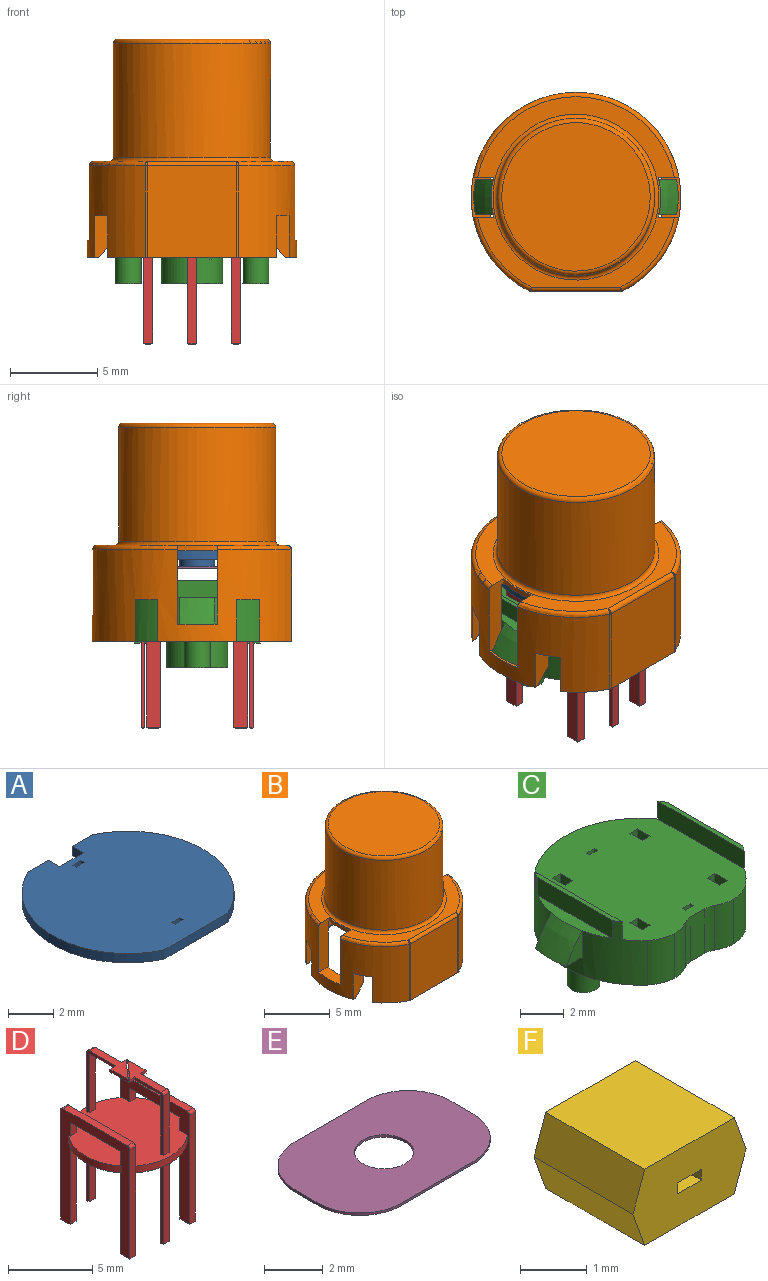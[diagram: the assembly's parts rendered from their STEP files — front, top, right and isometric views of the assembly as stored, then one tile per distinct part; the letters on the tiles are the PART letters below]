
ASSEMBLY  parts=6 mates=10
PART A: 20 faces, bbox 9.4x8.5x1 mm
  f0: plane 0.5x0.5mm, normal (0,1,0), area 0.3mm2, adj f1,f15,f16,f17
  f1: plane 0.5x0.2mm, normal (1,0,0), area 0.1mm2, adj f0,f2,f16,f17
  f2: plane 0.5x0.5mm, normal (0,-1,0), area 0.3mm2, adj f1,f15,f16,f17
  f3: plane 0.5x0.2mm, normal (1,0,0), area 0.1mm2, adj f4,f13,f16,f17
  f4: plane 0.5x0.5mm, normal (0,-1,0), area 0.3mm2, adj f3,f5,f16,f17
  f5: plane 0.5x0.2mm, normal (-1,0,0), area 0.1mm2, adj f4,f13,f16,f17
  f6: plane 1.26x0.5mm, normal (0,1,0), area 0.6mm2, adj f7,f14,f16,f17
  f7: plane 0.7x0.5mm, normal (-1,0,0), area 0.4mm2, adj f6,f8,f16,f17
  f8: plane 1.5x0.5mm, normal (0,1,0), area 0.8mm2, adj f7,f9,f16,f17
  f9: plane 0.7x0.5mm, normal (1,0,0), area 0.4mm2, adj f8,f10,f16,f17
  f10: plane 1.26x0.5mm, normal (0,1,0), area 0.6mm2, adj f9,f11,f16,f17
  f11: cylinder r=4.7mm len=8.5mm, axis (0,0,-1), area 5.3mm2, adj f10,f12,f16,f17
  f12: plane 4x0.5mm, normal (0,-1,0), area 2mm2, adj f11,f14,f16,f17
  f13: plane 0.5x0.5mm, normal (0,1,0), area 0.3mm2, adj f3,f5,f16,f17
  f14: cylinder r=4.7mm len=8.5mm, axis (0,0,-1), area 5.3mm2, adj f6,f12,f16,f17
  f15: plane 0.5x0.2mm, normal (-1,0,0), area 0.1mm2, adj f0,f2,f16,f17
  f16: plane 9.4x8.5mm, normal (0,0,1), area 65.7mm2, adj f0,f1,f2,f3,f4,f5,f6,f7
  f17: plane 9.4x8.5mm, normal (0,0,-1), area 62.6mm2, adj f0,f1,f2,f3,f4,f5,f6,f7
  f18: cylinder r=1mm len=2mm, axis (0,0,1), area 3.1mm2, adj f17,f19
  f19: plane 2x2mm, normal (0,0,-1), area 3.1mm2, adj f18
PART B: 55 faces, bbox 12.8x12.4x12.6 mm
  f0: cylinder r=5mm len=4.2mm, axis (0,0,1), area 15.5mm2, adj f8,f10,f18,f22,f30,f34,f35,f36
  f1: cylinder r=5mm len=4.2mm, axis (0,0,1), area 15.5mm2, adj f6,f10,f13,f18,f29,f40,f41,f42
  f2: cylinder r=6mm len=12mm, axis (0,0,1), area 134.9mm2, adj f3,f4,f5,f12,f13,f16,f22,f23
  f3: plane 4.57x0.7mm, normal (0,0,-1), area 0.9mm2, adj f2,f8,f31,f35
  f4: plane 4.57x0.7mm, normal (0,0,-1), area 0.9mm2, adj f2,f6,f38,f41
  f5: plane 9.69x2.49mm, normal (0,0,-1), area 2.2mm2, adj f2,f7,f9,f32,f39
  f6: bspline ~5.22x1.33mm, area 6mm2, adj f1,f4,f11,f25,f38,f41
  f7: bspline ~4.58x2.74mm, area 5.9mm2, adj f5,f9,f11,f39
  f8: bspline ~5.22x1.33mm, area 6mm2, adj f0,f3,f11,f24,f31,f35
  f9: bspline ~4.58x2.74mm, area 5.9mm2, adj f5,f7,f11,f32
  f10: plane 4.75x4.2mm, normal (0,1,0), area 19.9mm2, adj f0,f1,f18,f28
  f11: cylinder r=5mm len=9.73mm, axis (0,0,1), area 44.7mm2, adj f6,f7,f8,f9,f12,f18,f23,f31
  f12: plane 4.52x1.2mm, normal (0,-1,0), area 4.6mm2, adj f2,f11,f17,f18,f25,f27,f51
  f13: plane 4.52x1.2mm, normal (0,1,0), area 4.6mm2, adj f1,f2,f17,f18,f25,f27,f45
  f14: cylinder r=3.5mm len=7mm, axis (0,0,1), area 138.5mm2, adj f18,f21
  f15: plane 5.25x5.11mm, normal (0,-1,0), area 26.9mm2, adj f16,f44,f47,f48
  f16: plane 9.7x1.9mm, normal (0,0,-1), area 2.1mm2, adj f2,f15,f28,f29,f30,f34,f42,f44
  f17: plane 11.27x10.9mm, normal (0,0,1), area 26.7mm2, adj f12,f13,f22,f23,f26,f27,f45,f48
  f18: plane 9.73x8.87mm, normal (0,0,-1), area 35.8mm2, adj f0,f1,f10,f11,f12,f13,f14,f22
  f19: cylinder r=4.5mm len=9mm, axis (0,0,-1), area 183.8mm2, adj f43,f52
  f20: plane 8.5x8.5mm, normal (0,0,1), area 56.7mm2, adj f43
  f21: plane 7x7mm, normal (0,0,-1), area 38.5mm2, adj f14
  f22: plane 4.52x1.2mm, normal (0,1,0), area 4.6mm2, adj f0,f2,f17,f18,f24,f26,f50
  f23: plane 4.52x1.2mm, normal (0,-1,0), area 4.6mm2, adj f2,f11,f17,f18,f24,f26,f51
  f24: plane 2.3x1.14mm, normal (0,0,1), area 2.3mm2, adj f2,f8,f22,f23
  f25: plane 2.3x1.14mm, normal (0,0,1), area 2.3mm2, adj f2,f6,f12,f13
  f26: cylinder r=4.85mm len=2.3mm, axis (0,0,1), area 0.7mm2, adj f17,f18,f22,f23
  f27: cylinder r=4.85mm len=2.3mm, axis (0,0,1), area 0.7mm2, adj f12,f13,f17,f18
  f28: plane 5.16x1mm, normal (0,0.78,-0.62), area 6.3mm2, adj f10,f16,f29,f30
  f29: bspline ~2.39x2.14mm, area 2.6mm2, adj f1,f16,f28,f42
  f30: bspline ~2.39x2.14mm, area 2.6mm2, adj f0,f16,f28,f34
  f31: plane 2.43x1.13mm, normal (0,1,0), area 2.2mm2, adj f2,f3,f8,f11,f33
  f32: plane 2.46x1.38mm, normal (0,-1,0), area 2.6mm2, adj f2,f5,f9,f11,f33
  f33: plane 2.04x1.3mm, normal (0,0,-1), area 1.5mm2, adj f2,f11,f31,f32
  f34: plane 2.46x1.38mm, normal (0,1,0), area 2.6mm2, adj f0,f2,f16,f30,f36
  f35: plane 2.43x1.13mm, normal (0,-1,0), area 2.2mm2, adj f0,f2,f3,f8,f36
  f36: plane 2.04x1.3mm, normal (0,0,-1), area 1.5mm2, adj f0,f2,f34,f35
  f37: plane 2.04x1.3mm, normal (0,0,-1), area 1.5mm2, adj f2,f11,f38,f39
  f38: plane 2.43x1.13mm, normal (0,1,0), area 2.2mm2, adj f2,f4,f6,f11,f37
  f39: plane 2.46x1.38mm, normal (0,-1,0), area 2.6mm2, adj f2,f5,f7,f11,f37
  f40: plane 2.04x1.3mm, normal (0,0,-1), area 1.5mm2, adj f1,f2,f41,f42
  f41: plane 2.43x1.13mm, normal (0,-1,0), area 2.2mm2, adj f1,f2,f4,f6,f40
  f42: plane 2.46x1.38mm, normal (0,1,0), area 2.6mm2, adj f1,f2,f16,f29,f40
  f43: torus R=4.25mm, axis (0,0,1), area 10.9mm2, adj f19,f20
  f44: cylinder r=0.25mm len=5.25mm, axis (0,0,1), area 0.6mm2, adj f2,f15,f16,f46
  f45: torus R=5.75mm, axis (0,0,-1), area 2.1mm2, adj f2,f13,f17,f46
  f46: sphere r=0.25mm, area 0mm2, adj f44,f45,f48
  f47: cylinder r=0.25mm len=5.25mm, axis (0,0,1), area 0.6mm2, adj f2,f15,f16,f49
  f48: cylinder r=0.25mm len=5.11mm, axis (-1,0,0), area 2mm2, adj f15,f17,f46,f49
  f49: sphere r=0.25mm, area 0mm2, adj f47,f48,f50
  f50: torus R=5.75mm, axis (0,0,-1), area 2.1mm2, adj f2,f17,f22,f49
  f51: torus R=5.75mm, axis (0,0,-1), area 6.4mm2, adj f2,f12,f17,f23
  f52: torus R=4.75mm, axis (0,0,-1), area 11.3mm2, adj f17,f19
  f53: plane 4.5x1.5mm, normal (0,-1,0), area 6.8mm2, adj f11,f18,f54
  f54: plane 4.5x0.54mm, normal (0,0,-1), area 1.6mm2, adj f11,f53
PART C: 92 faces, bbox 11.7x9x5 mm
  f0: plane 9x7.92mm, normal (0,0,1), area 62mm2, adj f2,f3,f4,f5,f6,f7,f8,f9
  f1: plane 4.85x0.65mm, normal (0,0,1), area 2.1mm2, adj f17,f18,f87
  f2: plane 1x0.5mm, normal (0,-1,0), area 0.5mm2, adj f0,f34,f36,f67
  f3: plane 1x0.5mm, normal (0,1,0), area 0.5mm2, adj f0,f38,f40,f67
  f4: plane 1x0.5mm, normal (0,1,0), area 0.5mm2, adj f0,f42,f44,f67
  f5: plane 1x0.5mm, normal (0,-1,0), area 0.5mm2, adj f0,f46,f48,f67
  f6: plane 1x0.5mm, normal (0,-1,0), area 0.5mm2, adj f0,f7,f9,f67
  f7: plane 1x0.2mm, normal (1,0,0), area 0.2mm2, adj f0,f6,f8,f67
  f8: plane 1x0.5mm, normal (0,1,0), area 0.5mm2, adj f0,f7,f9,f67
  f9: plane 1x0.2mm, normal (-1,0,0), area 0.2mm2, adj f0,f6,f8,f67
  f10: plane 1x0.5mm, normal (0,-1,0), area 0.5mm2, adj f0,f11,f13,f67
  f11: plane 1x0.2mm, normal (1,0,0), area 0.2mm2, adj f0,f10,f12,f67
  f12: plane 1x0.5mm, normal (0,1,0), area 0.5mm2, adj f0,f11,f13,f67
  f13: plane 1x0.2mm, normal (-1,0,0), area 0.2mm2, adj f0,f10,f12,f67
  f14: plane 2x1.1mm, normal (0,0,-1), area 2mm2, adj f15,f18,f60,f61
  f15: revolved ~2.41x1.5mm, area 3.7mm2, adj f14,f19,f60,f61
  f16: plane 2x1.1mm, normal (0,0,-1), area 2mm2, adj f17,f18,f58,f59
  f17: revolved ~2.41x1.5mm, area 3.7mm2, adj f1,f16,f58,f59
  f18: cylinder r=4.85mm len=9.7mm, axis (0,0,-1), area 54.6mm2, adj f0,f1,f14,f16,f19,f20,f28,f30
  f19: plane 4.85x0.65mm, normal (0,0,1), area 2.1mm2, adj f15,f18,f90
  f20: plane 9.7x9mm, normal (0,0,-1), area 55.3mm2, adj f18,f21,f23,f25,f27,f28,f29,f30
  f21: cylinder r=1.75mm len=3.5mm, axis (0,0,-1), area 16.5mm2, adj f20,f22
  f22: plane 3.5x3.5mm, normal (0,0,-1), area 9.6mm2, adj f21
  f23: cylinder r=0.75mm len=1.5mm, axis (0,0,-1), area 7.1mm2, adj f20,f24
  f24: plane 1.5x1.5mm, normal (0,0,-1), area 1.8mm2, adj f23
  f25: cylinder r=0.75mm len=1.5mm, axis (0,0,-1), area 7.1mm2, adj f20,f26
  f26: plane 1.5x1.5mm, normal (0,0,-1), area 1.8mm2, adj f25
  f27: plane 2.5x0.91mm, normal (0,-1,0), area 2.3mm2, adj f0,f20,f32,f33
  f28: cylinder r=2mm len=2.5mm, axis (0,0,-1), area 3.5mm2, adj f0,f18,f20,f29
  f29: cylinder r=2mm len=2.5mm, axis (0,0,1), area 2.5mm2, adj f0,f20,f28,f33
  f30: cylinder r=2mm len=2.5mm, axis (0,0,-1), area 3.5mm2, adj f0,f18,f20,f31
  f31: cylinder r=2mm len=2.5mm, axis (0,0,1), area 2.5mm2, adj f0,f20,f30,f32
  f32: cylinder r=1mm len=2.5mm, axis (0,0,1), area 1.3mm2, adj f0,f20,f27,f31
  f33: cylinder r=1mm len=2.5mm, axis (0,0,1), area 1.3mm2, adj f0,f20,f27,f29
  f34: plane 2.5x0.8mm, normal (1,0,0), area 1.7mm2, adj f0,f2,f20,f35,f37,f63,f66,f67
  f35: plane 2.5x0.5mm, normal (0,1,0), area 1.3mm2, adj f0,f20,f34,f36
  f36: plane 2.5x0.8mm, normal (-1,0,0), area 1.9mm2, adj f0,f2,f20,f35,f37,f62,f66,f67
  f37: plane 1x0.5mm, normal (0,-1,0), area 0.5mm2, adj f20,f34,f36,f66
  f38: plane 2.5x0.8mm, normal (1,0,0), area 1.7mm2, adj f0,f3,f20,f39,f41,f64,f66,f67
  f39: plane 1x0.5mm, normal (0,1,0), area 0.5mm2, adj f20,f38,f40,f66
  f40: plane 2.5x0.8mm, normal (-1,0,0), area 1.9mm2, adj f0,f3,f20,f39,f41,f62,f66,f67
  f41: plane 2.5x0.5mm, normal (0,-1,0), area 1.3mm2, adj f0,f20,f38,f40
  f42: plane 2.5x0.8mm, normal (1,0,0), area 1.9mm2, adj f0,f4,f20,f43,f45,f65,f66,f67
  f43: plane 1x0.5mm, normal (0,1,0), area 0.5mm2, adj f20,f42,f44,f66
  f44: plane 2.5x0.8mm, normal (-1,0,0), area 1.7mm2, adj f0,f4,f20,f43,f45,f64,f66,f67
  f45: plane 2.5x0.5mm, normal (0,-1,0), area 1.2mm2, adj f0,f20,f42,f44
  f46: plane 2.5x0.8mm, normal (1,0,0), area 1.9mm2, adj f0,f5,f20,f47,f49,f65,f66,f67
  f47: plane 2.5x0.5mm, normal (0,1,0), area 1.2mm2, adj f0,f20,f46,f48
  f48: plane 2.5x0.8mm, normal (-1,0,0), area 1.7mm2, adj f0,f5,f20,f47,f49,f63,f66,f67
  f49: plane 1x0.5mm, normal (0,-1,0), area 0.5mm2, adj f20,f46,f48,f66
  f50: plane 1x0.5mm, normal (0,-1,0), area 0.5mm2, adj f20,f51,f53,f66
  f51: plane 1x0.2mm, normal (1,0,0), area 0.2mm2, adj f20,f50,f52,f66
  f52: plane 1x0.5mm, normal (0,1,0), area 0.5mm2, adj f20,f51,f53,f66
  f53: plane 1x0.2mm, normal (-1,0,0), area 0.2mm2, adj f20,f50,f52,f66
  f54: plane 1x0.5mm, normal (0,-1,0), area 0.5mm2, adj f20,f55,f57,f66
  f55: plane 1x0.2mm, normal (1,0,0), area 0.2mm2, adj f20,f54,f56,f66
  f56: plane 1x0.5mm, normal (0,1,0), area 0.5mm2, adj f20,f55,f57,f66
  f57: plane 1x0.2mm, normal (-1,0,0), area 0.2mm2, adj f20,f54,f56,f66
  f58: plane 1.54x1.06mm, normal (0,-1,0), area 0.8mm2, adj f16,f17,f18
  f59: plane 1.54x1.06mm, normal (0,1,0), area 0.8mm2, adj f16,f17,f18
  f60: plane 1.54x1.06mm, normal (0,1,0), area 0.8mm2, adj f14,f15,f18
  f61: plane 1.54x1.06mm, normal (0,-1,0), area 0.8mm2, adj f14,f15,f18
  f62: cylinder r=3.54mm len=4.44mm, axis (0,0,1), area 2.4mm2, adj f36,f40,f66,f67
  f63: cylinder r=3.54mm len=4.5mm, axis (0,0,1), area 2.4mm2, adj f34,f48,f66,f67
  f64: cylinder r=3.54mm len=4.5mm, axis (0,0,1), area 2.4mm2, adj f38,f44,f66,f67
  f65: cylinder r=3.54mm len=4.44mm, axis (0,0,1), area 2.4mm2, adj f42,f46,f66,f67
  f66: plane 7.07x7.07mm, normal (0,0,1), area 38.3mm2, adj f34,f36,f37,f38,f39,f40,f42,f43
  f67: plane 7.07x7.07mm, normal (0,0,-1), area 38.3mm2, adj f2,f3,f4,f5,f6,f7,f8,f9
  f68: plane 0.1x0.1mm, normal (0,1,0), area 0mm2, adj f20,f69,f79,f80
  f69: plane 0.45x0.1mm, normal (1,0,0), area 0mm2, adj f20,f68,f70,f80
  f70: plane 0.45x0.1mm, normal (0,1,0), area 0mm2, adj f20,f69,f71,f80
  f71: plane 0.1x0.1mm, normal (1,0,0), area 0mm2, adj f20,f70,f72,f80
  f72: plane 0.45x0.1mm, normal (0,-1,0), area 0mm2, adj f20,f71,f73,f80
  f73: plane 0.45x0.1mm, normal (1,0,0), area 0mm2, adj f20,f72,f74,f80
  f74: plane 0.1x0.1mm, normal (0,-1,0), area 0mm2, adj f20,f73,f75,f80
  f75: plane 0.45x0.1mm, normal (-1,0,0), area 0mm2, adj f20,f74,f76,f80
  f76: plane 0.45x0.1mm, normal (0,-1,0), area 0mm2, adj f20,f75,f77,f80
  f77: plane 0.1x0.1mm, normal (-1,0,0), area 0mm2, adj f20,f76,f78,f80
  f78: plane 0.45x0.1mm, normal (0,1,0), area 0mm2, adj f20,f77,f79,f80
  f79: plane 0.45x0.1mm, normal (-1,0,0), area 0mm2, adj f20,f68,f78,f80
  f80: plane 1x1mm, normal (0,0,-1), area 0.2mm2, adj f68,f69,f70,f71,f72,f73,f74,f75
  f81: plane 0.1x0.1mm, normal (0,1,0), area 0mm2, adj f20,f82,f84,f85
  f82: plane 1x0.1mm, normal (1,0,0), area 0.1mm2, adj f20,f81,f83,f85
  f83: plane 0.1x0.1mm, normal (0,-1,0), area 0mm2, adj f20,f82,f84,f85
  f84: plane 1x0.1mm, normal (-1,0,0), area 0.1mm2, adj f20,f81,f83,f85
  f85: plane 1x0.1mm, normal (0,0,-1), area 0.1mm2, adj f81,f82,f83,f84
  f86: plane 5.6x1mm, normal (-1,0,0), area 5.6mm2, adj f0,f18,f88
  f87: plane 4.85x1mm, normal (1,0,0), area 4.9mm2, adj f1,f18,f88
  f88: plane 5.6x0.24mm, normal (0,0,1), area 1.3mm2, adj f18,f86,f87
  f89: plane 5.6x1mm, normal (1,0,0), area 5.6mm2, adj f0,f18,f91
  f90: plane 4.85x1mm, normal (-1,0,0), area 4.9mm2, adj f18,f19,f91
  f91: plane 5.6x0.24mm, normal (0,0,1), area 1.3mm2, adj f18,f89,f90
PART D: 92 faces, bbox 7.1x7.1x11 mm
  f0: plane 7.07x7.07mm, normal (0,0,-1), area 38.3mm2, adj f1,f2,f3,f4,f5,f7,f12,f14
  f1: cylinder r=3.54mm len=4.44mm, axis (0,0,1), area 2.4mm2, adj f0,f9,f12
  f2: cylinder r=3.54mm len=4.5mm, axis (0,0,1), area 2.4mm2, adj f0,f5,f9,f14
  f3: cylinder r=3.54mm len=4.5mm, axis (0,0,1), area 2.4mm2, adj f0,f5,f9,f14
  f4: cylinder r=3.54mm len=4.44mm, axis (0,0,1), area 2.4mm2, adj f0,f7,f9
  f5: plane 8.1x5.8mm, normal (-1,0,0), area 15.3mm2, adj f0,f2,f3,f6,f8,f9,f10,f11
  f6: plane 7.9x0.5mm, normal (0,-1,0), area 4mm2, adj f5,f7,f45,f86
  f7: plane 8.1x5.8mm, normal (1,0,0), area 15.8mm2, adj f0,f4,f6,f8,f9,f10,f11,f26
  f8: plane 1x0.5mm, normal (0,1,0), area 0.5mm2, adj f5,f7,f9,f71
  f9: plane 7.07x7.07mm, normal (0,0,1), area 38.3mm2, adj f1,f2,f3,f4,f5,f7,f8,f10
  f10: plane 1x0.5mm, normal (0,-1,0), area 0.5mm2, adj f5,f7,f9,f71
  f11: plane 7.9x0.5mm, normal (0,1,0), area 4mm2, adj f5,f7,f50,f87
  f12: plane 8.1x5.8mm, normal (-1,0,0), area 15.8mm2, adj f0,f1,f9,f13,f15,f16,f17,f30
  f13: plane 1x0.5mm, normal (0,-1,0), area 0.5mm2, adj f9,f12,f14,f70
  f14: plane 8.1x5.8mm, normal (1,0,0), area 15.3mm2, adj f0,f2,f3,f9,f13,f15,f16,f17
  f15: plane 7.9x0.5mm, normal (0,1,0), area 3.9mm2, adj f12,f14,f54,f89
  f16: plane 7.9x0.5mm, normal (0,-1,0), area 3.9mm2, adj f12,f14,f57,f88
  f17: plane 1x0.5mm, normal (0,1,0), area 0.5mm2, adj f9,f12,f14,f70
  f18: plane 4.25x0.5mm, normal (0,1,0), area 2.1mm2, adj f9,f19,f21,f91
  f19: plane 4.5x2.4mm, normal (-1,0,0), area 1.3mm2, adj f9,f18,f20,f72,f73,f74,f85,f91
  f20: plane 4.3x0.5mm, normal (0,-1,0), area 2.1mm2, adj f9,f19,f21,f85
  f21: plane 4.5x2.4mm, normal (1,0,0), area 1.3mm2, adj f9,f18,f20,f72,f73,f75,f85,f91
  f22: plane 4.3x0.5mm, normal (0,1,0), area 2.1mm2, adj f9,f23,f25,f84
  f23: plane 4.5x2.4mm, normal (-1,0,0), area 1.3mm2, adj f9,f22,f24,f78,f79,f83,f84,f90
  f24: plane 4.25x0.5mm, normal (0,-1,0), area 2.1mm2, adj f9,f23,f25,f90
  f25: plane 4.5x2.4mm, normal (1,0,0), area 1.3mm2, adj f9,f22,f24,f78,f82,f83,f84,f90
  f26: plane 5.9x0.5mm, normal (0,1,0), area 3mm2, adj f0,f5,f7,f46
  f27: plane 0.6x0.3mm, normal (0,0,-1), area 0.2mm2, adj f44,f45,f46,f47
  f28: plane 5.9x0.5mm, normal (0,-1,0), area 3mm2, adj f0,f5,f7,f49
  f29: plane 0.6x0.3mm, normal (0,0,-1), area 0.2mm2, adj f48,f49,f50,f51
  f30: plane 5.9x0.5mm, normal (0,-1,0), area 2.9mm2, adj f0,f12,f14,f53
  f31: plane 0.6x0.3mm, normal (0,0,-1), area 0.2mm2, adj f52,f53,f54,f55
  f32: plane 5.9x0.5mm, normal (0,1,0), area 2.9mm2, adj f0,f12,f14,f58
  f33: plane 0.6x0.3mm, normal (0,0,-1), area 0.2mm2, adj f56,f57,f58,f59
  f34: plane 5.95x0.5mm, normal (0,1,0), area 3mm2, adj f0,f35,f37,f61
  f35: plane 5.95x0.2mm, normal (-1,0,0), area 1.2mm2, adj f0,f34,f36,f60
  f36: plane 5.95x0.5mm, normal (0,-1,0), area 3mm2, adj f0,f35,f37,f62
  f37: plane 5.95x0.2mm, normal (1,0,0), area 1.2mm2, adj f0,f34,f36,f63
  f38: plane 0.4x0.1mm, normal (0,0,-1), area 0mm2, adj f60,f61,f62,f63
  f39: plane 5.95x0.5mm, normal (0,1,0), area 3mm2, adj f0,f40,f42,f65
  f40: plane 5.95x0.2mm, normal (-1,0,0), area 1.2mm2, adj f0,f39,f41,f64
  f41: plane 5.95x0.5mm, normal (0,-1,0), area 3mm2, adj f0,f40,f42,f66
  f42: plane 5.95x0.2mm, normal (1,0,0), area 1.2mm2, adj f0,f39,f41,f67
  f43: plane 0.4x0.1mm, normal (0,0,-1), area 0mm2, adj f64,f65,f66,f67
  f44: plane 0.8x0.1mm, normal (-0.71,0,-0.71), area 0.1mm2, adj f5,f27,f45,f46
  f45: plane 0.5x0.1mm, normal (0,-0.71,-0.71), area 0.1mm2, adj f6,f27,f44,f47
  f46: plane 0.5x0.1mm, normal (0,0.71,-0.71), area 0.1mm2, adj f26,f27,f44,f47
  f47: plane 0.8x0.1mm, normal (0.71,0,-0.71), area 0.1mm2, adj f7,f27,f45,f46
  f48: plane 0.8x0.1mm, normal (-0.71,0,-0.71), area 0.1mm2, adj f5,f29,f49,f50
  f49: plane 0.5x0.1mm, normal (0,-0.71,-0.71), area 0.1mm2, adj f28,f29,f48,f51
  f50: plane 0.5x0.1mm, normal (0,0.71,-0.71), area 0.1mm2, adj f11,f29,f48,f51
  f51: plane 0.8x0.1mm, normal (0.71,0,-0.71), area 0.1mm2, adj f7,f29,f49,f50
  f52: plane 0.8x0.1mm, normal (-0.71,0,-0.71), area 0.1mm2, adj f12,f31,f53,f54
  f53: plane 0.5x0.1mm, normal (0,-0.71,-0.71), area 0.1mm2, adj f30,f31,f52,f55
  f54: plane 0.5x0.1mm, normal (0,0.71,-0.71), area 0.1mm2, adj f15,f31,f52,f55
  f55: plane 0.8x0.1mm, normal (0.71,0,-0.71), area 0.1mm2, adj f14,f31,f53,f54
  f56: plane 0.8x0.1mm, normal (-0.71,0,-0.71), area 0.1mm2, adj f12,f33,f57,f58
  f57: plane 0.5x0.1mm, normal (0,-0.71,-0.71), area 0.1mm2, adj f16,f33,f56,f59
  f58: plane 0.5x0.1mm, normal (0,0.71,-0.71), area 0.1mm2, adj f32,f33,f56,f59
  f59: plane 0.8x0.1mm, normal (0.71,0,-0.71), area 0.1mm2, adj f14,f33,f57,f58
  f60: plane 0.2x0.05mm, normal (-0.71,0,-0.71), area 0mm2, adj f35,f38,f61,f62
  f61: plane 0.5x0.05mm, normal (0,0.71,-0.71), area 0mm2, adj f34,f38,f60,f63
  f62: plane 0.5x0.05mm, normal (0,-0.71,-0.71), area 0mm2, adj f36,f38,f60,f63
  f63: plane 0.2x0.05mm, normal (0.71,0,-0.71), area 0mm2, adj f37,f38,f61,f62
  f64: plane 0.2x0.05mm, normal (-0.71,0,-0.71), area 0mm2, adj f40,f43,f65,f66
  f65: plane 0.5x0.05mm, normal (0,0.71,-0.71), area 0mm2, adj f39,f43,f64,f67
  f66: plane 0.5x0.05mm, normal (0,-0.71,-0.71), area 0mm2, adj f41,f43,f64,f67
  f67: plane 0.2x0.05mm, normal (0.71,0,-0.71), area 0mm2, adj f42,f43,f65,f66
  f68: plane 5.4x0.5mm, normal (0,0,1), area 2.7mm2, adj f5,f7,f86,f87
  f69: plane 5.4x0.5mm, normal (0,0,1), area 2.7mm2, adj f12,f14,f88,f89
  f70: plane 4.2x0.5mm, normal (0,0,-1), area 2.1mm2, adj f12,f13,f14,f17
  f71: plane 4.2x0.5mm, normal (0,0,-1), area 2.1mm2, adj f5,f7,f8,f10
  f72: plane 3.67x1.35mm, normal (0,0,-1), area 2.1mm2, adj f19,f21,f74,f75,f76,f77,f91
  f73: plane 3.72x1.35mm, normal (0,0,1), area 2.1mm2, adj f19,f21,f74,f75,f76,f77,f85
  f74: plane 0.39x0.2mm, normal (0,-1,0), area 0.1mm2, adj f19,f72,f73,f76
  f75: plane 0.46x0.2mm, normal (0,-1,0), area 0.1mm2, adj f21,f72,f73,f77
  f76: plane 1.52x1.35mm, normal (-0.75,0.66,0), area 0.4mm2, adj f72,f73,f74,f77
  f77: plane 1.52x0.2mm, normal (1,0,0), area 0.3mm2, adj f72,f73,f75,f76
  f78: plane 3.72x1.35mm, normal (0,0,1), area 2.1mm2, adj f23,f25,f79,f80,f81,f82,f84
  f79: plane 0.46x0.2mm, normal (0,1,0), area 0.1mm2, adj f23,f78,f80,f83
  f80: plane 1.52x0.2mm, normal (-1,0,0), area 0.3mm2, adj f78,f79,f81,f83
  f81: plane 1.52x1.35mm, normal (0.75,-0.66,0), area 0.4mm2, adj f78,f80,f82,f83
  f82: plane 0.39x0.2mm, normal (0,1,0), area 0.1mm2, adj f25,f78,f81,f83
  f83: plane 3.67x1.35mm, normal (0,0,-1), area 2.1mm2, adj f23,f25,f79,f80,f81,f82,f90
  f84: cylinder r=0.2mm len=0.5mm, axis (-1,0,0), area 0.2mm2, adj f22,f23,f25,f78
  f85: cylinder r=0.2mm len=0.5mm, axis (-1,0,0), area 0.2mm2, adj f19,f20,f21,f73
  f86: cylinder r=0.2mm len=0.5mm, axis (1,0,0), area 0.2mm2, adj f5,f6,f7,f68
  f87: cylinder r=0.2mm len=0.5mm, axis (-1,0,0), area 0.2mm2, adj f5,f7,f11,f68
  f88: cylinder r=0.2mm len=0.5mm, axis (1,0,0), area 0.2mm2, adj f12,f14,f16,f69
  f89: cylinder r=0.2mm len=0.5mm, axis (-1,0,0), area 0.2mm2, adj f12,f14,f15,f69
  f90: cylinder r=0.05mm len=0.5mm, axis (1,0,0), area 0mm2, adj f23,f24,f25,f83
  f91: cylinder r=0.05mm len=0.5mm, axis (-1,0,0), area 0mm2, adj f18,f19,f21,f72
PART E: 11 faces, bbox 7.4x5.1x0.1 mm
  f0: plane 1.1x0.1mm, normal (1,0,0), area 0.1mm2, adj f5,f6,f7,f10
  f1: plane 3.42x0.1mm, normal (0,-1,0), area 0.3mm2, adj f5,f6,f7,f8
  f2: plane 1.1x0.1mm, normal (-1,0,0), area 0.1mm2, adj f5,f6,f8,f9
  f3: plane 3.42x0.1mm, normal (0,1,0), area 0.3mm2, adj f5,f6,f9,f10
  f4: cylinder r=1mm len=2mm, axis (0,0,-1), area 0.6mm2, adj f5,f6
  f5: plane 7.42x5.1mm, normal (0,0,1), area 31.3mm2, adj f0,f1,f2,f3,f4,f7,f8,f9
  f6: plane 7.42x5.1mm, normal (0,0,-1), area 31.3mm2, adj f0,f1,f2,f3,f4,f7,f8,f9
  f7: cylinder r=2mm len=2mm, axis (0,0,1), area 0.3mm2, adj f0,f1,f5,f6
  f8: cylinder r=2mm len=2mm, axis (0,0,-1), area 0.3mm2, adj f1,f2,f5,f6
  f9: cylinder r=2mm len=2mm, axis (0,0,1), area 0.3mm2, adj f2,f3,f5,f6
  f10: cylinder r=2mm len=2mm, axis (0,0,-1), area 0.3mm2, adj f0,f3,f5,f6
PART F: 24 faces, bbox 2.4x2.1x1.4 mm
  f0: plane 2.4x1.4mm, normal (0,-1,0), area 2.9mm2, adj f1,f2,f4,f5,f6,f7,f8,f9
  f1: plane 2.1x1.9mm, normal (0,0,1), area 4mm2, adj f0,f3,f5,f6
  f2: plane 2.1x1.9mm, normal (0,0,-1), area 4mm2, adj f0,f3,f4,f7
  f3: plane 2.4x1.4mm, normal (0,1,0), area 2.9mm2, adj f1,f2,f4,f5,f6,f7,f12,f13
  f4: plane 2.1x0.7mm, normal (-0.94,0,-0.34), area 1.6mm2, adj f0,f2,f3,f6
  f5: plane 2.1x0.7mm, normal (0.94,0,0.34), area 1.6mm2, adj f0,f1,f3,f7
  f6: plane 2.1x0.7mm, normal (-0.94,0,0.34), area 1.6mm2, adj f0,f1,f3,f4
  f7: plane 2.1x0.7mm, normal (0.94,0,-0.34), area 1.6mm2, adj f0,f2,f3,f5
  f8: plane 0.25x0.2mm, normal (1,0,0), area 0mm2, adj f0,f9,f11,f20
  f9: plane 1.77x1.35mm, normal (0,0,1), area 1.2mm2, adj f0,f8,f10,f20,f21,f22,f23
  f10: plane 0.25x0.2mm, normal (-1,0,0), area 0mm2, adj f0,f9,f11,f21
  f11: plane 1.77x1.35mm, normal (0,0,-1), area 1.2mm2, adj f0,f8,f10,f20,f21,f22,f23
  f12: plane 0.25x0.2mm, normal (1,0,0), area 0mm2, adj f3,f13,f15,f16
  f13: plane 1.77x1.35mm, normal (0,0,-1), area 1.2mm2, adj f3,f12,f14,f16,f17,f18,f19
  f14: plane 0.25x0.2mm, normal (-1,0,0), area 0mm2, adj f3,f13,f15,f19
  f15: plane 1.77x1.35mm, normal (0,0,1), area 1.2mm2, adj f3,f12,f14,f16,f17,f18,f19
  f16: plane 0.46x0.2mm, normal (0,-1,0), area 0.1mm2, adj f12,f13,f15,f17
  f17: plane 1.52x0.2mm, normal (1,0,0), area 0.3mm2, adj f13,f15,f16,f18
  f18: plane 1.52x1.35mm, normal (-0.75,0.66,0), area 0.4mm2, adj f13,f15,f17,f19
  f19: plane 0.39x0.2mm, normal (0,-1,0), area 0.1mm2, adj f13,f14,f15,f18
  f20: plane 0.39x0.2mm, normal (0,1,0), area 0.1mm2, adj f8,f9,f11,f22
  f21: plane 0.46x0.2mm, normal (0,1,0), area 0.1mm2, adj f9,f10,f11,f23
  f22: plane 1.52x1.35mm, normal (0.75,-0.66,0), area 0.4mm2, adj f9,f11,f20,f23
  f23: plane 1.52x0.2mm, normal (-1,0,0), area 0.3mm2, adj f9,f11,f21,f22
PLACE A at identity
PLACE B at identity
PLACE C at identity fixed
PLACE D at identity
PLACE E at identity
PLACE F at identity
MATE planar A.f11 <-> B.f0  axis (0,0,1) through (2.5,-2.5,6.7)mm
MATE planar D.f16 <-> C.f47  axis (0,-1,0) through (0,-5.4,0.55)mm
MATE planar D.f74 <-> F.f20  axis (0,-1,0) through (2.05,-3.3,7.4)mm
MATE slider A.f11 <-> C.f18  axis (0,0,-1) through (2.5,-2.5,6.45)mm
MATE planar D.f70 <-> C.f0  axis (0,0,-1) through (0,-2.5,4)mm
MATE fastened E.f4 <-> A.f11  axis (0,0,-1) through (2.5,-2.5,5.7)mm
MATE slider B.f0 <-> A.f11  axis (0,0,-1) through (2.5,-2.5,10.5)mm
MATE planar D.f7 <-> C.f36  axis (1,0,0) through (5.25,-2.5,1.32)mm
MATE planar F.f23 <-> D.f77  axis (-1,0,0) through (3.21,-2.54,7.4)mm
MATE planar D.f78 <-> F.f11  axis (0,0,1) through (2.47,-2.46,7.5)mm
